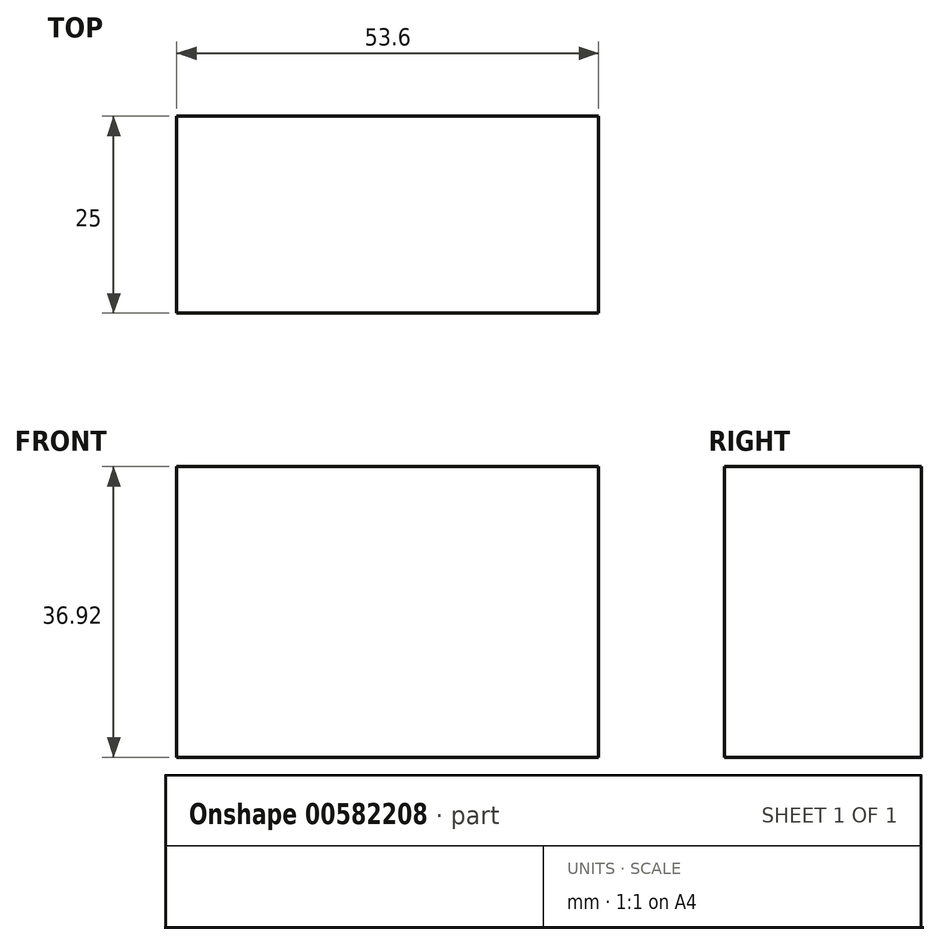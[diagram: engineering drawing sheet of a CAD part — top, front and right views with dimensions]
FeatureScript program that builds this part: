
annotation { "Feature Type Name" : "Feature", "Feature Type Description" : "" }
export const myFeature = defineFeature(function(context is Context, id is Id, definition is map)
    precondition{}
    {
        {
            var Q0;
            Q0=qCreatedBy(makeId("Front.planeOp"),FACE);
            var sketch = newSketch(context, id + "F0", { "sketchPlane" : qUnion([Q0])});
            skLineSegment(sketch, "E0.bottom", {"start": v(-79.84, 27.5) * mm, "end": v(-26.24, 27.5) * mm});
            skLineSegment(sketch, "E0.top", {"start": v(-79.84, -9.43) * mm, "end": v(-26.24, -9.43) * mm});
            skLineSegment(sketch, "E0.left", {"start": v(-79.84, 27.5) * mm, "end": v(-79.84, -9.43) * mm});
            skLineSegment(sketch, "E0.right", {"start": v(-26.24, 27.5) * mm, "end": v(-26.24, -9.43) * mm});
            skSolve(sketch);
        }
        {
            var Q0;
            Q0=makeQuery(id+"F0.imprint","IMPRINT",FACE,{"disambiguationData":[TD([[makeQuery(id+"F0.imprint","IMPRINT",EDGE,{"derivedFrom":sQuery(id+"F0.wireOp",EDGE,"E0.bottom")}),-1.0]])]});
            extrude(context, id + "F1", {"entities" : qUnion([Q0]), "depth" : 25 * mm, "offsetDistance" : 25 * mm});
        }
        {
            var Q0;
            Q0=qCreatedBy(makeId("Right.planeOp"),FACE);
            var sketch = newSketch(context, id + "F2", { "sketchPlane" : qUnion([Q0])});
            skCircle(sketch, "E1", {"center": v(-17.71, 34.01) * mm, "radius": 36.6 * mm});
            skSolve(sketch);
        }
        {
            var Q0;
            Q0=sQuery(id+"F2.wireOp",EDGE,"E1");
            var Q1;
            Q1=makeQuery(id+"F1.opExtrude","CAP_EDGE",EDGE,{"disambiguationData":[OSD([sQuery(id+"F0.wireOp",EDGE,"E0.right")])],"isStart":true});
            revolve(context, id + "F3", {"bodyType" : ToolBodyType.SURFACE, "surfaceEntities" : qUnion([Q0]), "axis" : qUnion([Q1]), "revolveType" : RevolveType.FULL});
        }
    });
